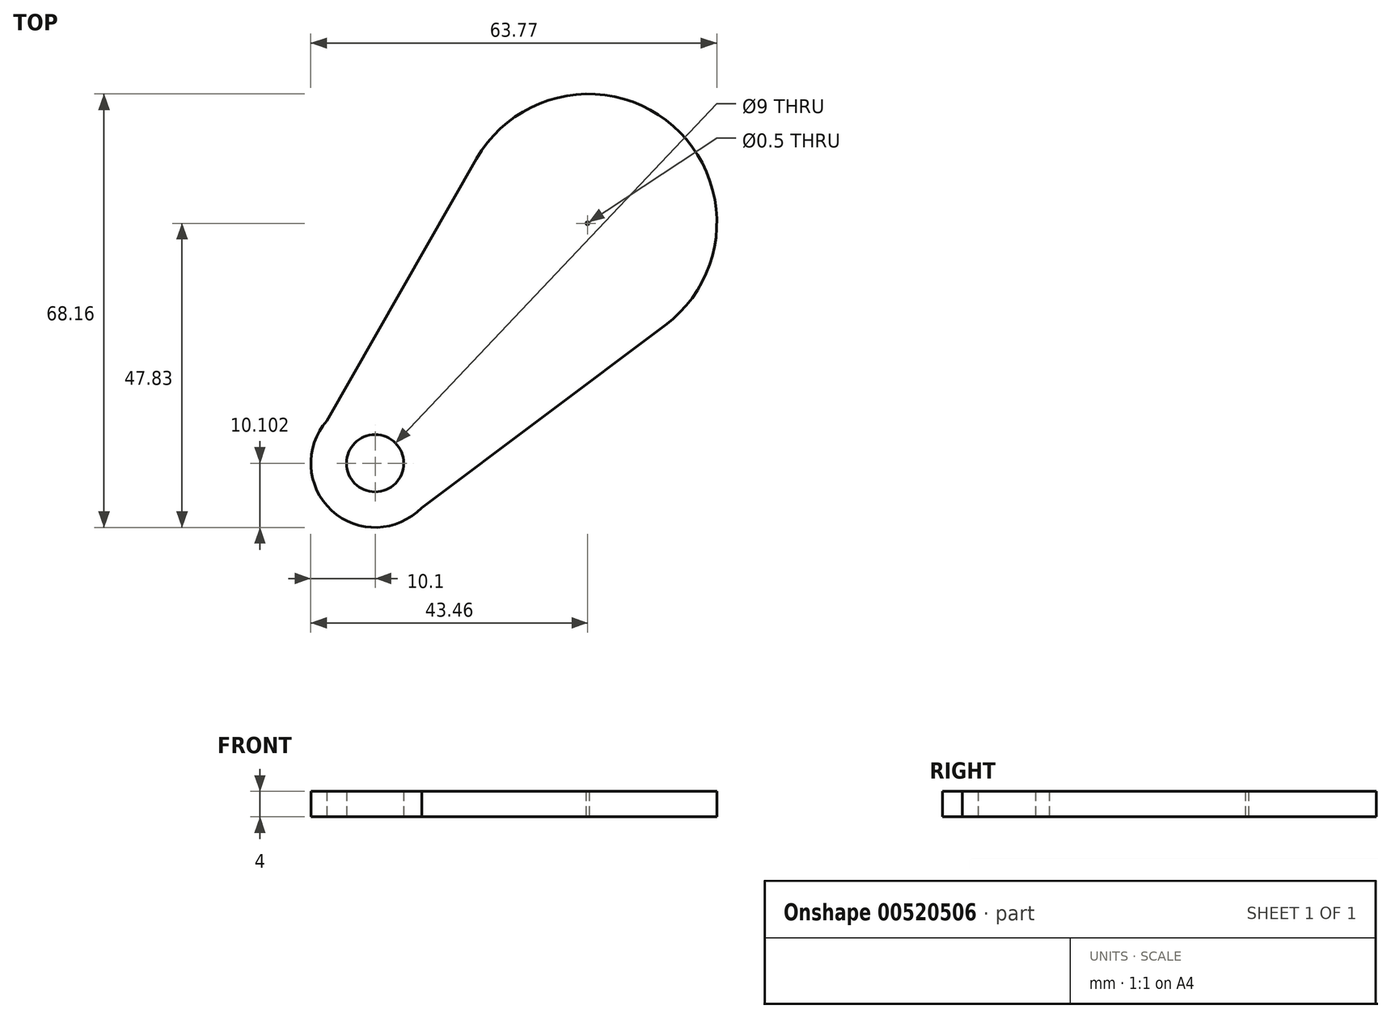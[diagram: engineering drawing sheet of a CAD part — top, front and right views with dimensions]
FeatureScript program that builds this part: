
annotation { "Feature Type Name" : "Feature", "Feature Type Description" : "" }
export const myFeature = defineFeature(function(context is Context, id is Id, definition is map)
    precondition{}
    {
        {
            var Q0;
            Q0=qCreatedBy(makeId("Top.planeOp"),FACE);
            var sketch = newSketch(context, id + "F0", { "sketchPlane" : qUnion([Q0])});
            skLineSegment(sketch, "E0", {"start": v(-40.93, -31.05) * mm, "end": v(-17.43, 10.14) * mm});
            skLineSegment(sketch, "E1", {"start": v(-26.05, -44.7) * mm, "end": v(12.22, -16.03) * mm});
            skArc(sketch, "E2", {"start": v(12.22, -16.03) * mm, "mid": v(13.48, 15.27) * mm, "end": v(-17.43, 10.14) * mm});
            skArc(sketch, "E3", {"start": v(-40.93, -31.05) * mm, "mid": v(-40.19, -45.17) * mm, "end": v(-26.05, -44.7) * mm});
            skCircle(sketch, "E4", {"center": v(-33.36, -37.73) * mm, "radius": 4.5 * mm});
            skCircle(sketch, "E5", {"center": v(0, 0) * mm, "radius": 0.25 * mm});
            skSolve(sketch);
        }
        {
            var Q0;
            Q0=makeQuery(id+"F0.imprint","IMPRINT",FACE,{"disambiguationData":[TD([[makeQuery(id+"F0.imprint","IMPRINT",EDGE,{"derivedFrom":sQuery(id+"F0.wireOp",EDGE,"E0")}),-1.0]])]});
            extrude(context, id + "F1", {"entities" : qUnion([Q0]), "depth" : 4 * mm, "offsetDistance" : 25 * mm});
        }
    });
